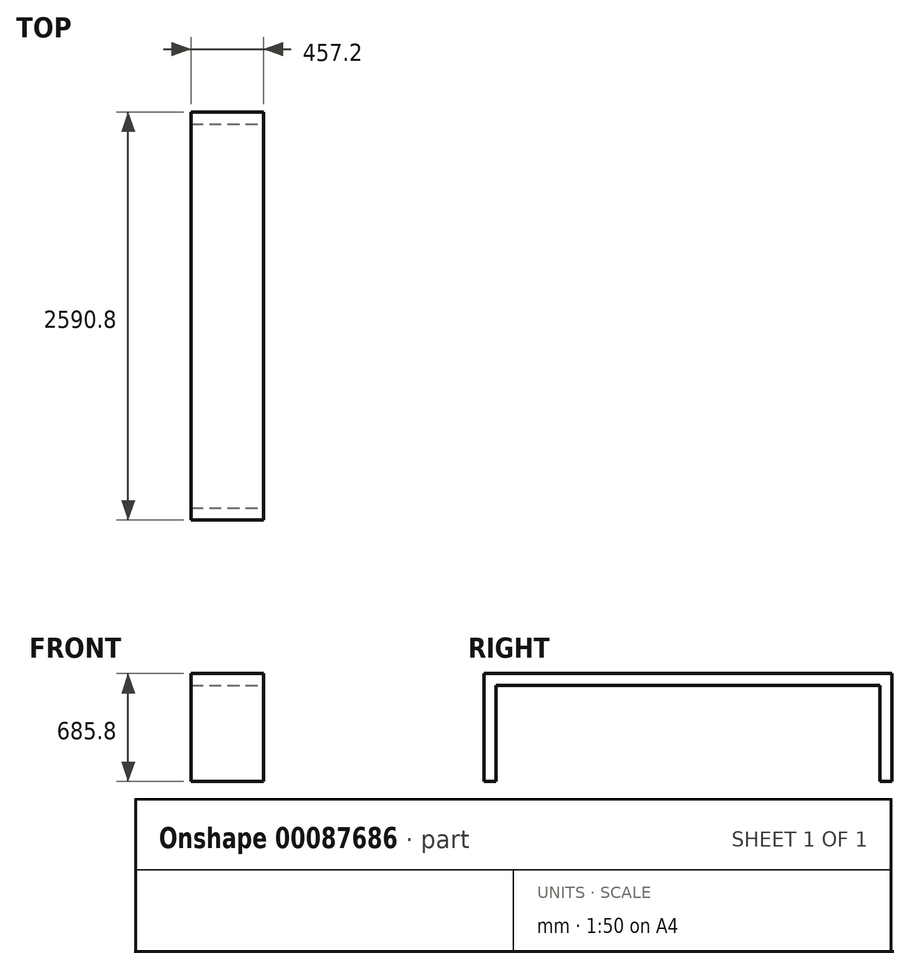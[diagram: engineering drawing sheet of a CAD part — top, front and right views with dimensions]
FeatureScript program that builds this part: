
annotation { "Feature Type Name" : "Feature", "Feature Type Description" : "" }
export const myFeature = defineFeature(function(context is Context, id is Id, definition is map)
    precondition{}
    {
        {
            var Q0;
            Q0=qCreatedBy(makeId("Top.planeOp"),FACE);
            var sketch = newSketch(context, id + "F0", { "sketchPlane" : qUnion([Q0])});
            skLineSegment(sketch, "E0.bottom", {"start": v(-2897.27, 86.59) * mm, "end": v(-2440.07, 86.59) * mm});
            skLineSegment(sketch, "E0.top", {"start": v(-2897.27, -2351.81) * mm, "end": v(-2440.07, -2351.81) * mm});
            skLineSegment(sketch, "E0.left", {"start": v(-2897.27, 86.59) * mm, "end": v(-2897.27, -2351.81) * mm});
            skLineSegment(sketch, "E0.right", {"start": v(-2440.07, 86.59) * mm, "end": v(-2440.07, -2351.81) * mm});
            skSolve(sketch);
        }
        {
            var Q0;
            Q0=qSketchRegion(id+"F0",true);
            extrude(context, id + "F1", {"entities" : qUnion([Q0]), "depth" : 609.6 * mm});
        }
        {
            var Q0;
            Q0=makeQuery(id+"F1.opExtrude","SWEPT_FACE",FACE,{"disambiguationData":[OSD([sQuery(id+"F0.wireOp",EDGE,"E0.right")])]});
            var Q1;
            Q1=makeQuery(id+"F1.opExtrude","SWEPT_FACE",FACE,{"disambiguationData":[OSD([sQuery(id+"F0.wireOp",EDGE,"E0.left")])]});
            var Q2;
            Q2=makeQuery(id+"F1.opExtrude","CAP_FACE",FACE,{"disambiguationData":[OSD([sQuery(id+"F0.wireOp",EDGE,"E0.bottom"),sQuery(id+"F0.wireOp",EDGE,"E0.top"),sQuery(id+"F0.wireOp",EDGE,"E0.left"),sQuery(id+"F0.wireOp",EDGE,"E0.right")])],"isStart":true});
            shell(context, id + "F2", {"entities" : qUnion([Q0, Q1, Q2]), "thickness" : 76.2 * mm, "oppositeDirection" : true});
        }
    });
